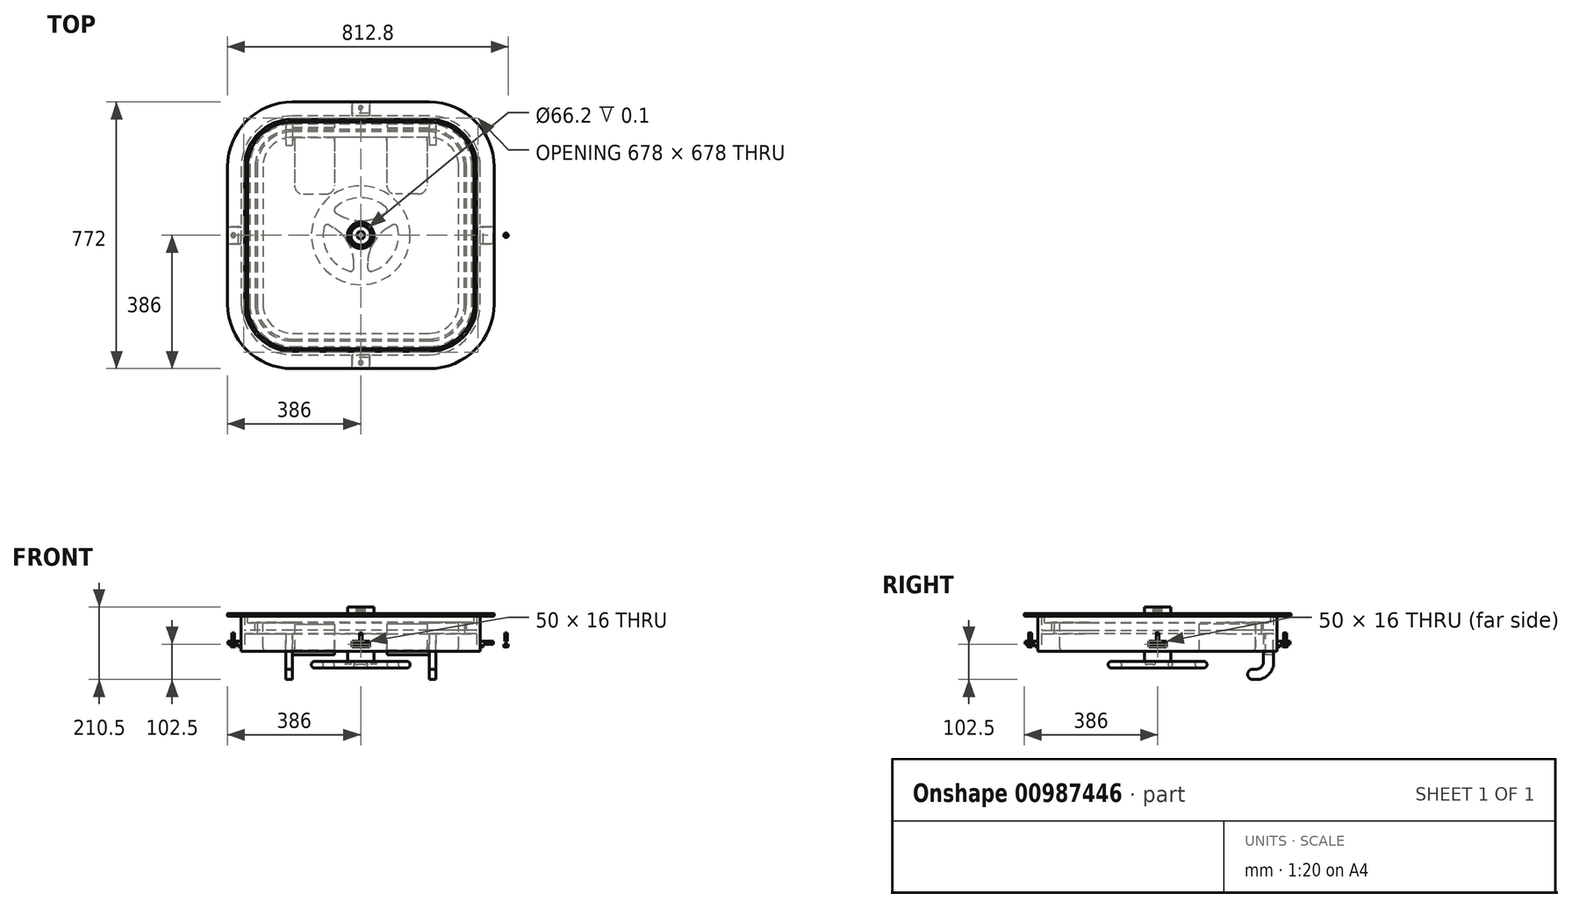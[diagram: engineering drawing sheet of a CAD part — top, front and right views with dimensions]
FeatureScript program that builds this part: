
annotation { "Feature Type Name" : "Feature", "Feature Type Description" : "" }
export const myFeature = defineFeature(function(context is Context, id is Id, definition is map)
    precondition{}
    {
        {
            var Q0;
            Q0=qCreatedBy(makeId("Top.planeOp"),FACE);
            var sketch = newSketch(context, id + "F0", { "sketchPlane" : qUnion([Q0])});
            skPoint(sketch, "E0.middle", {"position": v(0, 0) * mm});
            skPoint(sketch, "E1.visualSharp", {"position": v(-397.3, 343.3) * mm});
            skPoint(sketch, "E2.visualSharp", {"position": v(397.3, 343.3) * mm});
            skPoint(sketch, "E3.visualSharp", {"position": v(397.3, -343.3) * mm});
            skPoint(sketch, "E4.visualSharp", {"position": v(-397.3, -343.3) * mm});
            skLineSegment(sketch, "E5.1", {"start": v(-198.4, -300) * mm, "end": v(198.4, -300) * mm});
            skLineSegment(sketch, "E5.2", {"start": v(-300, -198.4) * mm, "end": v(-300, 198.4) * mm});
            skLineSegment(sketch, "E5.5", {"start": v(-198.4, 300) * mm, "end": v(198.4, 300) * mm});
            skLineSegment(sketch, "E5.7", {"start": v(300, -198.4) * mm, "end": v(300, 198.4) * mm});
            skPoint(sketch, "E6.visualSharp", {"position": v(300, -300) * mm});
            skArc(sketch, "E6.filletArc", {"start": v(198.4, -300) * mm, "mid": v(270.24, -270.24) * mm, "end": v(300, -198.4) * mm});
            skPoint(sketch, "E7.visualSharp", {"position": v(-300, -300) * mm});
            skArc(sketch, "E7.filletArc", {"start": v(-300, -198.4) * mm, "mid": v(-270.24, -270.24) * mm, "end": v(-198.4, -300) * mm});
            skPoint(sketch, "E8.visualSharp", {"position": v(-300, 300) * mm});
            skArc(sketch, "E8.filletArc", {"start": v(-198.4, 300) * mm, "mid": v(-270.24, 270.24) * mm, "end": v(-300, 198.4) * mm});
            skPoint(sketch, "E9.visualSharp", {"position": v(300, 300) * mm});
            skArc(sketch, "E9.filletArc", {"start": v(300, 198.4) * mm, "mid": v(270.24, 270.24) * mm, "end": v(198.4, 300) * mm});
            skLineSegment(sketch, "E10", {"start": v(198.4, -198.4) * mm, "end": v(-198.4, 198.4) * mm});
            skLineSegment(sketch, "E11", {"start": v(-198.4, -198.4) * mm, "end": v(198.4, 198.4) * mm});
            skSolve(sketch);
        }
        {
            var Q0;
            Q0=qCreatedBy(makeId("Front.planeOp"),FACE);
            var sketch = newSketch(context, id + "F1", { "sketchPlane" : qUnion([Q0])});
            skLineSegment(sketch, "E12", {"start": v(-346, 0) * mm, "end": v(-384, 0) * mm});
            skLineSegment(sketch, "E13", {"start": v(-386, 2) * mm, "end": v(-386, 6) * mm});
            skLineSegment(sketch, "E14", {"start": v(-384, 8) * mm, "end": v(-339, 8) * mm});
            skLineSegment(sketch, "E15", {"start": v(-336, 5) * mm, "end": v(-336, -38) * mm});
            skLineSegment(sketch, "E16", {"start": v(-333, -41) * mm, "end": v(-309, -41) * mm});
            skLineSegment(sketch, "E17", {"start": v(-306, -38) * mm, "end": v(-306, -19) * mm});
            skLineSegment(sketch, "E18", {"start": v(-303, -16) * mm, "end": v(-303, -16) * mm});
            skLineSegment(sketch, "E19", {"start": v(-300, -19) * mm, "end": v(-300, -48) * mm});
            skLineSegment(sketch, "E20", {"start": v(-303, -51) * mm, "end": v(-334, -51) * mm});
            skLineSegment(sketch, "E21", {"start": v(-336, -53) * mm, "end": v(-336, -99) * mm});
            skLineSegment(sketch, "E22", {"start": v(-339, -102) * mm, "end": v(-346, -102) * mm});
            skLineSegment(sketch, "E23", {"start": v(-346, -102) * mm, "end": v(-346, 0) * mm});
            skLineSegment(sketch, "E24", {"start": v(-300, -16) * mm, "end": v(-300, 0) * mm});
            skPoint(sketch, "E25.visualSharp", {"position": v(-300, -16) * mm});
            skArc(sketch, "E25.filletArc", {"start": v(-300, -19) * mm, "mid": v(-300.88, -16.88) * mm, "end": v(-303, -16) * mm});
            skPoint(sketch, "E26.visualSharp", {"position": v(-306, -16) * mm});
            skArc(sketch, "E26.filletArc", {"start": v(-303, -16) * mm, "mid": v(-305.12, -16.88) * mm, "end": v(-306, -19) * mm});
            skPoint(sketch, "E27.visualSharp", {"position": v(-306, -41) * mm});
            skArc(sketch, "E27.filletArc", {"start": v(-309, -41) * mm, "mid": v(-306.88, -40.12) * mm, "end": v(-306, -38) * mm});
            skPoint(sketch, "E28.visualSharp", {"position": v(-336, -41) * mm});
            skArc(sketch, "E28.filletArc", {"start": v(-336, -38) * mm, "mid": v(-335.12, -40.12) * mm, "end": v(-333, -41) * mm});
            skPoint(sketch, "E29.visualSharp", {"position": v(-300, -51) * mm});
            skArc(sketch, "E29.filletArc", {"start": v(-303, -51) * mm, "mid": v(-300.88, -50.12) * mm, "end": v(-300, -48) * mm});
            skPoint(sketch, "E30.visualSharp", {"position": v(-336, 8) * mm});
            skArc(sketch, "E30.filletArc", {"start": v(-336, 5) * mm, "mid": v(-336.88, 7.12) * mm, "end": v(-339, 8) * mm});
            skPoint(sketch, "E31.visualSharp", {"position": v(-336, -102) * mm});
            skArc(sketch, "E31.filletArc", {"start": v(-339, -102) * mm, "mid": v(-336.88, -101.12) * mm, "end": v(-336, -99) * mm});
            skPoint(sketch, "E32.visualSharp", {"position": v(-386, 8) * mm});
            skArc(sketch, "E32.filletArc", {"start": v(-384, 8) * mm, "mid": v(-385.41, 7.41) * mm, "end": v(-386, 6) * mm});
            skPoint(sketch, "E33.visualSharp", {"position": v(-386, 0) * mm});
            skArc(sketch, "E33.filletArc", {"start": v(-386, 2) * mm, "mid": v(-385.41, 0.59) * mm, "end": v(-384, 0) * mm});
            skPoint(sketch, "E34.visualSharp", {"position": v(-336, -51) * mm});
            skArc(sketch, "E34.filletArc", {"start": v(-334, -51) * mm, "mid": v(-335.41, -51.59) * mm, "end": v(-336, -53) * mm});
            skSolve(sketch);
        }
        {
            var Q0;
            Q0=makeQuery(id+"F1.imprint","IMPRINT",FACE,{"disambiguationData":[TD([[makeQuery(id+"F1.imprint","IMPRINT",EDGE,{"derivedFrom":sQuery(id+"F1.wireOp",EDGE,"E12")}),-1.0]])]});
            var Q1;
            Q1=sQuery(id+"F0.wireOp",EDGE,"E5.2");
            var Q2;
            Q2=sQuery(id+"F0.wireOp",EDGE,"E7.filletArc");
            var Q3;
            Q3=sQuery(id+"F0.wireOp",EDGE,"E5.1");
            var Q4;
            Q4=sQuery(id+"F0.wireOp",EDGE,"E6.filletArc");
            var Q5;
            Q5=sQuery(id+"F0.wireOp",EDGE,"E5.7");
            var Q6;
            Q6=sQuery(id+"F0.wireOp",EDGE,"E9.filletArc");
            var Q7;
            Q7=sQuery(id+"F0.wireOp",EDGE,"E5.5");
            var Q8;
            Q8=sQuery(id+"F0.wireOp",EDGE,"E8.filletArc");
            sweep(context, id + "F2", {"profiles" : qUnion([Q0]), "path" : qUnion([Q1, Q2, Q3, Q4, Q5, Q6, Q7, Q8])});
        }
        {
            var Q0;
            Q0=makeQuery(id+"F2.opSweep","SWEPT_FACE",FACE,{"disambiguationData":[OSD([sQuery(id+"F0.wireOp",EDGE,"E0.left"),sQuery(id+"F1.wireOp",EDGE,"E14")])]});
            var sketch = newSketch(context, id + "F3", { "sketchPlane" : qUnion([Q0])});
            skLineSegment(sketch, "E35.0", {"start": v(198.4, 328) * mm, "end": v(-198.4, 328) * mm});
            skArc(sketch, "E35.1", {"start": v(328, 198.4) * mm, "mid": v(290.04, 290.04) * mm, "end": v(198.4, 328) * mm});
            skArc(sketch, "E35.2", {"start": v(-198.4, 328) * mm, "mid": v(-290.04, 290.04) * mm, "end": v(-328, 198.4) * mm});
            skLineSegment(sketch, "E35.3", {"start": v(328, -198.4) * mm, "end": v(328, 198.4) * mm});
            skLineSegment(sketch, "E35.4", {"start": v(-328, 198.4) * mm, "end": v(-328, -198.4) * mm});
            skArc(sketch, "E35.5", {"start": v(-328, -198.4) * mm, "mid": v(-290.04, -290.04) * mm, "end": v(-198.4, -328) * mm});
            skLineSegment(sketch, "E35.6", {"start": v(-198.4, -328) * mm, "end": v(198.4, -328) * mm});
            skArc(sketch, "E35.7", {"start": v(198.4, -328) * mm, "mid": v(290.04, -290.04) * mm, "end": v(328, -198.4) * mm});
            skSolve(sketch);
        }
        {
            var Q0;
            Q0 = qSketchRegion(id + "F3", true);
            extrude(context, id + "F4", {"entities" : qUnion([Q0]), "oppositeDirection" : true, "depth" : 27 * mm, "offsetDistance" : 25 * mm});
        }
        {
            var Q0;
            Q0=qCreatedBy(makeId("Front.planeOp"),FACE);
            var sketch = newSketch(context, id + "F5", { "sketchPlane" : qUnion([Q0])});
            skLineSegment(sketch, "E36.0", {"start": v(346, -73) * mm, "end": v(346, -89) * mm});
            skLineSegment(sketch, "E37.0", {"start": v(-346, -73) * mm, "end": v(-346, -89) * mm});
            skLineSegment(sketch, "E38", {"start": v(346, -73) * mm, "end": v(384, -73) * mm});
            skLineSegment(sketch, "E39", {"start": v(384, -73) * mm, "end": v(384, -81) * mm});
            skLineSegment(sketch, "E40", {"start": v(384, -81) * mm, "end": v(354, -81) * mm});
            skLineSegment(sketch, "E41", {"start": v(354, -81) * mm, "end": v(354, -89) * mm});
            skLineSegment(sketch, "E42", {"start": v(354, -89) * mm, "end": v(346, -89) * mm});
            skLineSegment(sketch, "E43", {"start": v(-346, -73) * mm, "end": v(-384, -73) * mm});
            skLineSegment(sketch, "E44", {"start": v(-384, -73) * mm, "end": v(-384, -81) * mm});
            skLineSegment(sketch, "E45", {"start": v(-384, -81) * mm, "end": v(-354, -81) * mm});
            skLineSegment(sketch, "E46", {"start": v(-354, -81) * mm, "end": v(-354, -89) * mm});
            skLineSegment(sketch, "E47", {"start": v(-354, -89) * mm, "end": v(-346, -89) * mm});
            skPoint(sketch, "E48.orphan", {"position": v(-346, 0) * mm});
            skPoint(sketch, "E49.orphan", {"position": v(-346, -102) * mm});
            skPoint(sketch, "E50.orphan", {"position": v(346, 0) * mm});
            skPoint(sketch, "E51.orphan", {"position": v(346, -102) * mm});
            skSolve(sketch);
        }
        {
            var Q0;
            Q0 = qSketchRegion(id + "F5", true);
            extrude(context, id + "F6", {"entities" : qUnion([Q0]), "operationType" : NewBodyOperationType.ADD, "depth" : 25 * mm, "offsetDistance" : 25 * mm, "hasSecondDirection" : true, "secondDirectionOppositeDirection" : true, "secondDirectionDepth" : 25 * mm});
        }
        {
            var Q0;
            Q0=qCreatedBy(makeId("Right.planeOp"),FACE);
            var sketch = newSketch(context, id + "F7", { "sketchPlane" : qUnion([Q0])});
            skLineSegment(sketch, "E52.0", {"start": v(-346, 0) * mm, "end": v(-346, -102) * mm});
            skLineSegment(sketch, "E53.0", {"start": v(346, 0) * mm, "end": v(346, -102) * mm});
            skLineSegment(sketch, "E54", {"start": v(-346, -73) * mm, "end": v(-384, -73) * mm});
            skLineSegment(sketch, "E55", {"start": v(-384, -73) * mm, "end": v(-384, -81) * mm});
            skLineSegment(sketch, "E56", {"start": v(-384, -81) * mm, "end": v(-354, -81) * mm});
            skLineSegment(sketch, "E57", {"start": v(-354, -81) * mm, "end": v(-354, -89) * mm});
            skLineSegment(sketch, "E58", {"start": v(-354, -89) * mm, "end": v(-346, -89) * mm});
            skLineSegment(sketch, "E59", {"start": v(346, -73) * mm, "end": v(384, -73) * mm});
            skLineSegment(sketch, "E60", {"start": v(384, -73) * mm, "end": v(384, -81) * mm});
            skLineSegment(sketch, "E61", {"start": v(384, -81) * mm, "end": v(354, -81) * mm});
            skLineSegment(sketch, "E62", {"start": v(354, -81) * mm, "end": v(354, -89) * mm});
            skLineSegment(sketch, "E63", {"start": v(354, -89) * mm, "end": v(346, -89) * mm});
            skSolve(sketch);
        }
        {
            var Q0;
            Q0 = qSketchRegion(id + "F7", true);
            extrude(context, id + "F8", {"entities" : qUnion([Q0]), "operationType" : NewBodyOperationType.ADD, "depth" : 25 * mm, "offsetDistance" : 25 * mm, "hasSecondDirection" : true, "secondDirectionOppositeDirection" : true, "secondDirectionDepth" : 25 * mm});
        }
        {
            var Q0;
            Q0=makeQuery(id+"F8.opExtrude","SWEPT_FACE",FACE,{"disambiguationData":[OSD([sQuery(id+"F7.wireOp",EDGE,"E56")])]});
            var sketch = newSketch(context, id + "F9", { "sketchPlane" : qUnion([Q0])});
            skCircle(sketch, "E64", {"center": v(0, 369) * mm, "radius": 6.5 * mm});
            skPoint(sketch, "E64.centerSnap0", {"position": v(-25, 369) * mm});
            skPoint(sketch, "E64.centerSnap1", {"position": v(0, 384) * mm});
            skLineSegment(sketch, "E65", {"start": v(-369, 25) * mm, "end": v(-369, 0) * mm});
            skCircle(sketch, "E66", {"center": v(-369, 0) * mm, "radius": 6.5 * mm});
            skLineSegment(sketch, "E67", {"start": v(-300, 0) * mm, "end": v(0, 0) * mm});
            skCircle(sketch, "E68.MirrorC", {"center": v(420.3, 0) * mm, "radius": 6.5 * mm});
            skCircle(sketch, "E69.MirrorC", {"center": v(0, -369) * mm, "radius": 6.5 * mm});
            skLineSegment(sketch, "E70", {"start": v(0, 0) * mm, "end": v(0, 300) * mm});
            skSolve(sketch);
        }
        {
            var Q0;
            Q0 = qSketchRegion(id + "F9", true);
            extrude(context, id + "F10", {"entities" : qUnion([Q0]), "operationType" : NewBodyOperationType.ADD, "depth" : 8 * mm, "offsetDistance" : 25 * mm});
        }
        {
            var Q0;
            Q0=makeQuery(id+"F10.opExtrude","CAP_EDGE",EDGE,{"disambiguationData":[OSD([sQuery(id+"F9.wireOp",EDGE,"E66")])],"isStart":false});
            var Q1;
            Q1=makeQuery(id+"F10.opExtrude","CAP_EDGE",EDGE,{"disambiguationData":[OSD([sQuery(id+"F9.wireOp",EDGE,"E64")])],"isStart":false});
            var Q2;
            Q2=makeQuery(id+"F10.opExtrude","CAP_EDGE",EDGE,{"disambiguationData":[OSD([sQuery(id+"F9.wireOp",EDGE,"E68.MirrorC")])],"isStart":false});
            var Q3;
            Q3=makeQuery(id+"F10.opExtrude","CAP_EDGE",EDGE,{"disambiguationData":[OSD([sQuery(id+"F9.wireOp",EDGE,"E69.MirrorC")])],"isStart":false});
            chamfer(context, id + "F11", {"entities" : qUnion([Q0, Q1, Q2, Q3]), "width" : 1 * mm, "tangentPropagation" : true});
        }
        {
            var Q0;
            Q0=makeQuery(id+"F8.opExtrude","SWEPT_FACE",FACE,{"disambiguationData":[OSD([sQuery(id+"F7.wireOp",EDGE,"E59")])]});
            var sketch = newSketch(context, id + "F12", { "sketchPlane" : qUnion([Q0])});
            skCircle(sketch, "E71", {"center": v(0, 369) * mm, "radius": 4 * mm});
            skCircle(sketch, "E72", {"center": v(-369, 0) * mm, "radius": 4 * mm});
            skCircle(sketch, "E73", {"center": v(0, -369) * mm, "radius": 4 * mm});
            skCircle(sketch, "E74", {"center": v(420.3, 0) * mm, "radius": 4 * mm});
            skSolve(sketch);
        }
        {
            var Q0;
            Q0 = qSketchRegion(id + "F12", true);
            extrude(context, id + "F13", {"entities" : qUnion([Q0]), "operationType" : NewBodyOperationType.ADD, "depth" : 25 * mm, "offsetDistance" : 25 * mm});
        }
        {
            var Q0;
            Q0=makeQuery(id+"F4.opExtrude","CAP_FACE",FACE,{"disambiguationData":[OSD([sQuery(id+"F3.wireOp",EDGE,"E35.0"),sQuery(id+"F3.wireOp",EDGE,"E35.1"),sQuery(id+"F3.wireOp",EDGE,"E35.2"),sQuery(id+"F3.wireOp",EDGE,"E35.3"),sQuery(id+"F3.wireOp",EDGE,"E35.4"),sQuery(id+"F3.wireOp",EDGE,"E35.5"),sQuery(id+"F3.wireOp",EDGE,"E35.6"),sQuery(id+"F3.wireOp",EDGE,"E35.7")])],"isStart":false});
            shell(context, id + "F14", {"entities" : qUnion([Q0]), "thickness" : 6.35 * mm});
        }
        {
            var Q0;
            Q0=makeQuery(id+"F14.opShell","OFFSET_FACE",FACE,{"disambiguationData":[OSD([sQuery(id+"F3.wireOp",EDGE,"E35.0"),sQuery(id+"F3.wireOp",EDGE,"E35.1"),sQuery(id+"F3.wireOp",EDGE,"E35.2"),sQuery(id+"F3.wireOp",EDGE,"E35.3"),sQuery(id+"F3.wireOp",EDGE,"E35.4"),sQuery(id+"F3.wireOp",EDGE,"E35.5"),sQuery(id+"F3.wireOp",EDGE,"E35.6"),sQuery(id+"F3.wireOp",EDGE,"E35.7")])]});
            var sketch = newSketch(context, id + "F15", { "sketchPlane" : qUnion([Q0])});
            skLineSegment(sketch, "E75.0", {"start": v(-283.55, -198.4) * mm, "end": v(-283.55, 198.4) * mm});
            skArc(sketch, "E75.1", {"start": v(-198.4, -283.55) * mm, "mid": v(-258.61, -258.61) * mm, "end": v(-283.55, -198.4) * mm});
            skArc(sketch, "E75.2", {"start": v(-283.55, 198.4) * mm, "mid": v(-258.61, 258.61) * mm, "end": v(-198.4, 283.55) * mm});
            skLineSegment(sketch, "E75.3", {"start": v(198.4, -283.55) * mm, "end": v(-198.4, -283.55) * mm});
            skLineSegment(sketch, "E75.4", {"start": v(-198.4, 283.55) * mm, "end": v(198.4, 283.55) * mm});
            skArc(sketch, "E75.5", {"start": v(198.4, 283.55) * mm, "mid": v(258.61, 258.61) * mm, "end": v(283.55, 198.4) * mm});
            skLineSegment(sketch, "E75.6", {"start": v(283.55, 198.4) * mm, "end": v(283.55, -198.4) * mm});
            skArc(sketch, "E75.7", {"start": v(283.55, -198.4) * mm, "mid": v(258.61, -258.61) * mm, "end": v(198.4, -283.55) * mm});
            skSolve(sketch);
        }
        {
            var Q0;
            Q0 = qSketchRegion(id + "F15", true);
            extrude(context, id + "F16", {"entities" : qUnion([Q0]), "operationType" : NewBodyOperationType.ADD, "depth" : 102 * mm, "offsetDistance" : 25 * mm});
        }
        {
            var Q0;
            Q0=makeQuery(id+"F14.opShell","OFFSET_FACE",FACE,{"disambiguationData":[OSD([sQuery(id+"F3.wireOp",EDGE,"E35.0"),sQuery(id+"F3.wireOp",EDGE,"E35.1"),sQuery(id+"F3.wireOp",EDGE,"E35.2"),sQuery(id+"F3.wireOp",EDGE,"E35.3"),sQuery(id+"F3.wireOp",EDGE,"E35.4"),sQuery(id+"F3.wireOp",EDGE,"E35.5"),sQuery(id+"F3.wireOp",EDGE,"E35.6"),sQuery(id+"F3.wireOp",EDGE,"E35.7")])]});
            var sketch = newSketch(context, id + "F17", { "sketchPlane" : qUnion([Q0])});
            skLineSegment(sketch, "E76.0.0", {"start": v(198.4, 321.65) * mm, "end": v(-198.4, 321.65) * mm});
            skArc(sketch, "E76.0.1", {"start": v(-198.4, 321.65) * mm, "mid": v(-285.55, 285.55) * mm, "end": v(-321.65, 198.4) * mm});
            skLineSegment(sketch, "E76.0.2", {"start": v(-321.65, 198.4) * mm, "end": v(-321.65, -198.4) * mm});
            skArc(sketch, "E76.0.3", {"start": v(-321.65, -198.4) * mm, "mid": v(-285.55, -285.55) * mm, "end": v(-198.4, -321.65) * mm});
            skLineSegment(sketch, "E76.0.4", {"start": v(-198.4, -321.65) * mm, "end": v(198.4, -321.65) * mm});
            skArc(sketch, "E76.0.5", {"start": v(198.4, -321.65) * mm, "mid": v(285.55, -285.55) * mm, "end": v(321.65, -198.4) * mm});
            skLineSegment(sketch, "E76.0.6", {"start": v(321.65, -198.4) * mm, "end": v(321.65, 198.4) * mm});
            skArc(sketch, "E76.0.7", {"start": v(321.65, 198.4) * mm, "mid": v(285.55, 285.55) * mm, "end": v(198.4, 321.65) * mm});
            skLineSegment(sketch, "E77.0", {"start": v(-283.55, -198.4) * mm, "end": v(-283.55, 198.4) * mm});
            skArc(sketch, "E78.0", {"start": v(-198.4, -283.55) * mm, "mid": v(-258.61, -258.61) * mm, "end": v(-283.55, -198.4) * mm});
            skLineSegment(sketch, "E79.0", {"start": v(198.4, -283.55) * mm, "end": v(-198.4, -283.55) * mm});
            skArc(sketch, "E80.0", {"start": v(283.55, -198.4) * mm, "mid": v(258.61, -258.61) * mm, "end": v(198.4, -283.55) * mm});
            skLineSegment(sketch, "E81.0", {"start": v(283.55, 198.4) * mm, "end": v(283.55, -198.4) * mm});
            skArc(sketch, "E82.0", {"start": v(198.4, 283.55) * mm, "mid": v(258.61, 258.61) * mm, "end": v(283.55, 198.4) * mm});
            skLineSegment(sketch, "E83.0", {"start": v(-198.4, 283.55) * mm, "end": v(198.4, 283.55) * mm});
            skSolve(sketch);
        }
        {
            var Q0;
            Q0 = qSketchRegion(id + "F17", true);
            extrude(context, id + "F18", {"entities" : qUnion([Q0]), "operationType" : NewBodyOperationType.ADD, "depth" : 19 * mm, "offsetDistance" : 25 * mm});
        }
        {
            var Q0;
            Q0=makeQuery(id+"F16.opExtrude","CAP_FACE",FACE,{"disambiguationData":[OSD([sQuery(id+"F15.wireOp",EDGE,"E75.0"),sQuery(id+"F15.wireOp",EDGE,"E75.1"),sQuery(id+"F15.wireOp",EDGE,"E75.2"),sQuery(id+"F15.wireOp",EDGE,"E75.3"),sQuery(id+"F15.wireOp",EDGE,"E75.4"),sQuery(id+"F15.wireOp",EDGE,"E75.5"),sQuery(id+"F15.wireOp",EDGE,"E75.6"),sQuery(id+"F15.wireOp",EDGE,"E75.7")])],"isStart":false});
            var Q1;
            Q1=makeQuery(id+"F4.opExtrude","CAP_FACE",FACE,{"disambiguationData":[OSD([sQuery(id+"F3.wireOp",EDGE,"E35.0"),sQuery(id+"F3.wireOp",EDGE,"E35.1"),sQuery(id+"F3.wireOp",EDGE,"E35.2"),sQuery(id+"F3.wireOp",EDGE,"E35.3"),sQuery(id+"F3.wireOp",EDGE,"E35.4"),sQuery(id+"F3.wireOp",EDGE,"E35.5"),sQuery(id+"F3.wireOp",EDGE,"E35.6"),sQuery(id+"F3.wireOp",EDGE,"E35.7")])],"isStart":true});
            fillet(context, id + "F19", {"entities" : qUnion([Q0, Q1]), "radius" : 10 * mm, "tangentPropagation" : true, "allowEdgeOverflow" : false});
        }
        {
            var Q0;
            Q0=makeQuery(id+"F16.opExtrude","CAP_FACE",FACE,{"disambiguationData":[OSD([sQuery(id+"F15.wireOp",EDGE,"E75.0"),sQuery(id+"F15.wireOp",EDGE,"E75.1"),sQuery(id+"F15.wireOp",EDGE,"E75.2"),sQuery(id+"F15.wireOp",EDGE,"E75.3"),sQuery(id+"F15.wireOp",EDGE,"E75.4"),sQuery(id+"F15.wireOp",EDGE,"E75.5"),sQuery(id+"F15.wireOp",EDGE,"E75.6"),sQuery(id+"F15.wireOp",EDGE,"E75.7")])],"isStart":false});
            var sketch = newSketch(context, id + "F20", { "sketchPlane" : qUnion([Q0])});
            skLineSegment(sketch, "E84", {"start": v(0, -273.55) * mm, "end": v(0, 0) * mm});
            skLineSegment(sketch, "E85.bottom", {"start": v(-191.55, -283.55) * mm, "end": v(-75.55, -283.55) * mm});
            skLineSegment(sketch, "E85.top", {"start": v(-166.55, -119.55) * mm, "end": v(-100.55, -119.55) * mm});
            skLineSegment(sketch, "E85.left", {"start": v(-191.55, -283.55) * mm, "end": v(-191.55, -144.55) * mm});
            skLineSegment(sketch, "E85.right", {"start": v(-75.55, -283.55) * mm, "end": v(-75.55, -144.55) * mm});
            skPoint(sketch, "E86.visualSharp", {"position": v(-191.55, -119.55) * mm});
            skArc(sketch, "E86.filletArc", {"start": v(-166.55, -119.55) * mm, "mid": v(-184.23, -126.87) * mm, "end": v(-191.55, -144.55) * mm});
            skPoint(sketch, "E87.visualSharp", {"position": v(-75.55, -119.55) * mm});
            skArc(sketch, "E87.filletArc", {"start": v(-75.55, -144.55) * mm, "mid": v(-82.87, -126.87) * mm, "end": v(-100.55, -119.55) * mm});
            skLineSegment(sketch, "E88.MirrorCS", {"start": v(191.55, -283.55) * mm, "end": v(75.55, -283.55) * mm});
            skLineSegment(sketch, "E89.MirrorCS", {"start": v(75.55, -283.55) * mm, "end": v(75.55, -144.55) * mm});
            skArc(sketch, "E90.MirrorCS", {"start": v(75.55, -144.55) * mm, "mid": v(82.87, -126.87) * mm, "end": v(100.55, -119.55) * mm});
            skLineSegment(sketch, "E91.MirrorCS", {"start": v(166.55, -119.55) * mm, "end": v(100.55, -119.55) * mm});
            skArc(sketch, "E92.MirrorCS", {"start": v(166.55, -119.55) * mm, "mid": v(184.23, -126.87) * mm, "end": v(191.55, -144.55) * mm});
            skLineSegment(sketch, "E93.MirrorCS", {"start": v(191.55, -283.55) * mm, "end": v(191.55, -144.55) * mm});
            skSolve(sketch);
        }
        {
            var Q0;
            Q0 = qSketchRegion(id + "F20", true);
            extrude(context, id + "F21", {"entities" : qUnion([Q0]), "operationType" : NewBodyOperationType.REMOVE, "oppositeDirection" : true, "depth" : 78 * mm, "offsetDistance" : 25 * mm});
        }
        {
            var Q0;
            Q0=makeQuery(id+"F4.opExtrude","CAP_FACE",FACE,{"disambiguationData":[OSD([sQuery(id+"F3.wireOp",EDGE,"E35.0"),sQuery(id+"F3.wireOp",EDGE,"E35.1"),sQuery(id+"F3.wireOp",EDGE,"E35.2"),sQuery(id+"F3.wireOp",EDGE,"E35.3"),sQuery(id+"F3.wireOp",EDGE,"E35.4"),sQuery(id+"F3.wireOp",EDGE,"E35.5"),sQuery(id+"F3.wireOp",EDGE,"E35.6"),sQuery(id+"F3.wireOp",EDGE,"E35.7")])],"isStart":true});
            var sketch = newSketch(context, id + "F22", { "sketchPlane" : qUnion([Q0])});
            skCircle(sketch, "E94", {"center": v(0, 0) * mm, "radius": 38.1 * mm});
            skSolve(sketch);
        }
        {
            var Q0;
            Q0 = qSketchRegion(id + "F22", true);
            extrude(context, id + "F23", {"entities" : qUnion([Q0]), "operationType" : NewBodyOperationType.ADD, "depth" : 19 * mm, "offsetDistance" : 25 * mm});
        }
        {
            var Q0;
            Q0=makeQuery(id+"F23.opExtrude","CAP_FACE",FACE,{"disambiguationData":[OSD([sQuery(id+"F22.wireOp",EDGE,"E94")])],"isStart":false});
            var sketch = newSketch(context, id + "F24", { "sketchPlane" : qUnion([Q0])});
            skLineSegment(sketch, "E95.bottom", {"start": v(9, -9) * mm, "end": v(3.73, -9) * mm});
            skLineSegment(sketch, "E95.top", {"start": v(9, 9) * mm, "end": v(3.73, 9) * mm});
            skLineSegment(sketch, "E95.left", {"start": v(9, -9) * mm, "end": v(9, -3.73) * mm});
            skLineSegment(sketch, "E95.right", {"start": v(-9, -9) * mm, "end": v(-9, -3.73) * mm});
            skPoint(sketch, "E95.middle", {"position": v(0, 0) * mm});
            skLineSegment(sketch, "E96.bottom", {"start": v(12.73, 0) * mm, "end": v(9, -3.73) * mm});
            skLineSegment(sketch, "E96.top", {"start": v(0, 12.73) * mm, "end": v(-3.73, 9) * mm});
            skLineSegment(sketch, "E96.left", {"start": v(12.73, 0) * mm, "end": v(9, 3.73) * mm});
            skLineSegment(sketch, "E96.right", {"start": v(0, -12.73) * mm, "end": v(-3.73, -9) * mm});
            skLineSegment(sketch, "E97.trimOffspring", {"start": v(-9, 3.73) * mm, "end": v(-12.73, 0) * mm});
            skLineSegment(sketch, "E98.trimOffspring", {"start": v(-3.73, 9) * mm, "end": v(-9, 9) * mm});
            skLineSegment(sketch, "E99.trimOffspring", {"start": v(9, 3.73) * mm, "end": v(9, 9) * mm});
            skLineSegment(sketch, "E100.trimOffspring", {"start": v(3.73, -9) * mm, "end": v(0, -12.73) * mm});
            skLineSegment(sketch, "E101.trimOffspring", {"start": v(-3.73, -9) * mm, "end": v(-9, -9) * mm});
            skLineSegment(sketch, "E102.trimOffspring", {"start": v(-9, -3.73) * mm, "end": v(-12.73, 0) * mm});
            skLineSegment(sketch, "E103.trimOffspring", {"start": v(-9, 3.73) * mm, "end": v(-9, 9) * mm});
            skLineSegment(sketch, "E104.trimOffspring", {"start": v(3.73, 9) * mm, "end": v(0, 12.73) * mm});
            skSolve(sketch);
        }
        {
            var Q0;
            Q0 = qSketchRegion(id + "F24", true);
            extrude(context, id + "F25", {"entities" : qUnion([Q0]), "operationType" : NewBodyOperationType.REMOVE, "oppositeDirection" : true, "depth" : 18 * mm, "offsetDistance" : 25 * mm});
        }
        {
            var Q0;
            Q0=makeQuery(id+"F23.opExtrude","CAP_FACE",FACE,{"disambiguationData":[OSD([sQuery(id+"F22.wireOp",EDGE,"E94")])],"isStart":false});
            var sketch = newSketch(context, id + "F26", { "sketchPlane" : qUnion([Q0])});
            skCircle(sketch, "E105.0", {"center": v(0, 0) * mm, "radius": 33.1 * mm});
            skCircle(sketch, "E106", {"center": v(0, 0) * mm, "radius": 28.5 * mm});
            skSolve(sketch);
        }
        {
            var Q0;
            Q0 = qSketchRegion(id + "F26", true);
            extrude(context, id + "F27", {"entities" : qUnion([Q0]), "operationType" : NewBodyOperationType.REMOVE, "oppositeDirection" : true, "depth" : .1 * mm, "offsetDistance" : 25 * mm});
        }
        {
            var Q0;
            Q0=makeQuery(id+"F16.opExtrude","CAP_FACE",FACE,{"disambiguationData":[OSD([sQuery(id+"F15.wireOp",EDGE,"E75.0"),sQuery(id+"F15.wireOp",EDGE,"E75.1"),sQuery(id+"F15.wireOp",EDGE,"E75.2"),sQuery(id+"F15.wireOp",EDGE,"E75.3"),sQuery(id+"F15.wireOp",EDGE,"E75.4"),sQuery(id+"F15.wireOp",EDGE,"E75.5"),sQuery(id+"F15.wireOp",EDGE,"E75.6"),sQuery(id+"F15.wireOp",EDGE,"E75.7")])],"isStart":false});
            var sketch = newSketch(context, id + "F28", { "sketchPlane" : qUnion([Q0])});
            skCircle(sketch, "E107", {"center": v(0, 0) * mm, "radius": 38.1 * mm});
            skSolve(sketch);
        }
        {
            var Q0;
            Q0 = qSketchRegion(id + "F28", true);
            extrude(context, id + "F29", {"entities" : qUnion([Q0]), "operationType" : NewBodyOperationType.ADD, "depth" : 30.48 * mm, "offsetDistance" : 25 * mm});
        }
        {
            var Q0;
            Q0=makeQuery(id+"F29.opExtrude","CAP_FACE",FACE,{"disambiguationData":[OSD([sQuery(id+"F28.wireOp",EDGE,"E107")])],"isStart":false});
            var sketch = newSketch(context, id + "F30", { "sketchPlane" : qUnion([Q0])});
            skArc(sketch, "E108", {"start": v(-33.03, 103.87) * mm, "mid": v(-94.4, 54.5) * mm, "end": v(-106.47, -23.33) * mm});
            skCircle(sketch, "E109", {"center": v(0, 0) * mm, "radius": 143 * mm});
            skLineSegment(sketch, "E110", {"start": v(0, 109) * mm, "end": v(0, 0) * mm});
            skLineSegment(sketch, "E111", {"start": v(0, 0) * mm, "end": v(-94.4, -54.5) * mm});
            skLineSegment(sketch, "E112", {"start": v(-20, 94.35) * mm, "end": v(-20, 82.56) * mm});
            skLineSegment(sketch, "E113", {"start": v(-91.7, -29.85) * mm, "end": v(-81.5, -23.96) * mm});
            skArc(sketch, "E114", {"start": v(-81.5, -23.96) * mm, "mid": v(-36.48, 21.06) * mm, "end": v(-20, 82.56) * mm});
            skPoint(sketch, "E115.visualSharp", {"position": v(-20, 107.15) * mm});
            skArc(sketch, "E115.filletArc", {"start": v(-20, 94.35) * mm, "mid": v(-24.1, 102.42) * mm, "end": v(-33.03, 103.87) * mm});
            skPoint(sketch, "E116.visualSharp", {"position": v(-102.8, -36.25) * mm});
            skArc(sketch, "E116.filletArc", {"start": v(-106.47, -23.33) * mm, "mid": v(-100.74, -30.34) * mm, "end": v(-91.7, -29.85) * mm});
            skArc(sketch, "E117.1.0", {"start": v(-73.44, -80.54) * mm, "mid": v(0, -109) * mm, "end": v(73.44, -80.54) * mm});
            skArc(sketch, "E117.1.1", {"start": v(-71.7, -64.5) * mm, "mid": v(-76.65, -72.08) * mm, "end": v(-73.44, -80.54) * mm});
            skLineSegment(sketch, "E117.1.2", {"start": v(-71.7, -64.5) * mm, "end": v(-61.5, -58.6) * mm});
            skArc(sketch, "E117.1.3", {"start": v(61.5, -58.6) * mm, "mid": v(0, -42.12) * mm, "end": v(-61.5, -58.6) * mm});
            skLineSegment(sketch, "E117.1.4", {"start": v(71.7, -64.5) * mm, "end": v(61.5, -58.6) * mm});
            skArc(sketch, "E117.1.5", {"start": v(73.44, -80.54) * mm, "mid": v(76.65, -72.08) * mm, "end": v(71.7, -64.5) * mm});
            skArc(sketch, "E117.2.0", {"start": v(106.47, -23.33) * mm, "mid": v(94.4, 54.5) * mm, "end": v(33.03, 103.87) * mm});
            skArc(sketch, "E117.2.1", {"start": v(91.7, -29.85) * mm, "mid": v(100.74, -30.34) * mm, "end": v(106.47, -23.33) * mm});
            skLineSegment(sketch, "E117.2.2", {"start": v(91.7, -29.85) * mm, "end": v(81.5, -23.96) * mm});
            skArc(sketch, "E117.2.3", {"start": v(20, 82.56) * mm, "mid": v(36.48, 21.06) * mm, "end": v(81.5, -23.96) * mm});
            skLineSegment(sketch, "E117.2.4", {"start": v(20, 94.35) * mm, "end": v(20, 82.56) * mm});
            skArc(sketch, "E117.2.5", {"start": v(33.03, 103.87) * mm, "mid": v(24.1, 102.42) * mm, "end": v(20, 94.35) * mm});
            skSolve(sketch);
        }
        {
            var Q0;
            {var subQ0=sQuery(id+"F30.wireOp",EDGE,"E111");var subQ1=sQuery(id+"F30.wireOp",EDGE,"E110");var subQ2=makeQuery(id+"F30.imprint","INTERSECT",VERTEX,{"derivedFrom":[subQ1,subQ0]});Q0=makeQuery(id+"F30.imprint","IMPRINT",FACE,{"disambiguationData":[TD([[makeQuery(id+"F30.imprint","IMPRINT",EDGE,{"disambiguationData":[TD([[subQ2,1.0]])],"derivedFrom":subQ1}),-1.0]])]});}
            var Q1;
            {var subQ0=sQuery(id+"F30.wireOp",EDGE,"E111");var subQ1=sQuery(id+"F30.wireOp",EDGE,"E110");var subQ2=makeQuery(id+"F30.imprint","INTERSECT",VERTEX,{"derivedFrom":[subQ1,subQ0]});Q1=makeQuery(id+"F30.imprint","IMPRINT",FACE,{"disambiguationData":[TD([[makeQuery(id+"F30.imprint","IMPRINT",EDGE,{"disambiguationData":[TD([[subQ2,1.0]])],"derivedFrom":subQ1}),1.0]])]});}
            var Q2;
            Q2=makeQuery(id+"F30.imprint","IMPRINT",FACE,{"disambiguationData":[TD([[makeQuery(id+"F30.imprint","IMPRINT",EDGE,{"derivedFrom":sQuery(id+"F30.wireOp",EDGE,"E108")}),-1.0]])]});
            extrude(context, id + "F31", {"entities" : qUnion([Q0, Q1, Q2]), "operationType" : NewBodyOperationType.ADD, "depth" : 19 * mm, "offsetDistance" : 25 * mm});
        }
        {
            var Q0;
            Q0=makeQuery(id+"F31.opExtrude","CAP_EDGE",EDGE,{"disambiguationData":[OSD([sQuery(id+"F30.wireOp",EDGE,"E109")])],"isStart":true});
            var Q1;
            Q1=makeQuery(id+"F31.opExtrude","CAP_EDGE",EDGE,{"disambiguationData":[OSD([sQuery(id+"F30.wireOp",EDGE,"E117.2.0")])],"isStart":true});
            var Q2;
            Q2=makeQuery(id+"F31.opExtrude","CAP_EDGE",EDGE,{"disambiguationData":[OSD([sQuery(id+"F30.wireOp",EDGE,"E108")])],"isStart":true});
            var Q3;
            Q3=makeQuery(id+"F31.opExtrude","CAP_EDGE",EDGE,{"disambiguationData":[OSD([sQuery(id+"F30.wireOp",EDGE,"E117.1.3")])],"isStart":true});
            var Q4;
            Q4=makeQuery(id+"F31.opExtrude","CAP_FACE",FACE,{"disambiguationData":[OSD([sQuery(id+"F30.wireOp",EDGE,"E108"),sQuery(id+"F30.wireOp",EDGE,"E109"),sQuery(id+"F30.wireOp",EDGE,"E112"),sQuery(id+"F30.wireOp",EDGE,"E113"),sQuery(id+"F30.wireOp",EDGE,"E114"),sQuery(id+"F30.wireOp",EDGE,"E115.filletArc"),sQuery(id+"F30.wireOp",EDGE,"E116.filletArc"),sQuery(id+"F30.wireOp",EDGE,"E117.1.0"),sQuery(id+"F30.wireOp",EDGE,"E117.1.1"),sQuery(id+"F30.wireOp",EDGE,"E117.1.2"),sQuery(id+"F30.wireOp",EDGE,"E117.1.3"),sQuery(id+"F30.wireOp",EDGE,"E117.1.4"),sQuery(id+"F30.wireOp",EDGE,"E117.1.5"),sQuery(id+"F30.wireOp",EDGE,"E117.2.0"),sQuery(id+"F30.wireOp",EDGE,"E117.2.1"),sQuery(id+"F30.wireOp",EDGE,"E117.2.2"),sQuery(id+"F30.wireOp",EDGE,"E117.2.3"),sQuery(id+"F30.wireOp",EDGE,"E117.2.4"),sQuery(id+"F30.wireOp",EDGE,"E117.2.5")])],"isStart":false});
            fillet(context, id + "F32", {"entities" : qUnion([Q0, Q1, Q2, Q3, Q4]), "radius" : 9 * mm, "tangentPropagation" : true, "allowEdgeOverflow" : false});
        }
        {
            var Q0;
            Q0=makeQuery(id+"F2.opSweep","SWEPT_FACE",FACE,{"disambiguationData":[OSD([sQuery(id+"F0.wireOp",EDGE,"E5.2"),sQuery(id+"F1.wireOp",EDGE,"E20")])]});
            var sketch = newSketch(context, id + "F33", { "sketchPlane" : qUnion([Q0])});
            skLineSegment(sketch, "E118", {"start": v(0, 0) * mm, "end": v(0, -303) * mm});
            skLineSegment(sketch, "E119.bottom", {"start": v(-76.4, -336) * mm, "end": v(-198.4, -336) * mm});
            skLineSegment(sketch, "E119.top", {"start": v(-76.4, -312) * mm, "end": v(-198.4, -312) * mm});
            skLineSegment(sketch, "E119.left", {"start": v(-76.4, -336) * mm, "end": v(-76.4, -312) * mm});
            skLineSegment(sketch, "E119.right", {"start": v(-198.4, -336) * mm, "end": v(-198.4, -312) * mm});
            skLineSegment(sketch, "E120.MirrorCS", {"start": v(76.4, -336) * mm, "end": v(198.4, -336) * mm});
            skLineSegment(sketch, "E121.MirrorCS", {"start": v(76.4, -336) * mm, "end": v(76.4, -312) * mm});
            skLineSegment(sketch, "E122.MirrorCS", {"start": v(76.4, -312) * mm, "end": v(198.4, -312) * mm});
            skLineSegment(sketch, "E123.MirrorCS", {"start": v(198.4, -336) * mm, "end": v(198.4, -312) * mm});
            skSolve(sketch);
        }
        {
            var Q0;
            Q0 = qSketchRegion(id + "F33", true);
            extrude(context, id + "F34", {"entities" : qUnion([Q0]), "operationType" : NewBodyOperationType.ADD, "depth" : 61 * mm, "offsetDistance" : 25 * mm});
        }
        {
            var Q0;
            Q0=makeQuery(id+"F34.opExtrude","SWEPT_FACE",FACE,{"disambiguationData":[OSD([sQuery(id+"F33.wireOp",EDGE,"E119.right")])]});
            var sketch = newSketch(context, id + "F35", { "sketchPlane" : qUnion([Q0])});
            skArc(sketch, "E124.0", {"start": v(-336, -53) * mm, "mid": v(-335.41, -51.59) * mm, "end": v(-334, -51) * mm});
            skLineSegment(sketch, "E125.0", {"start": v(-334, -51) * mm, "end": v(-312, -51) * mm});
            skLineSegment(sketch, "E126.0.0", {"start": v(-306, -51) * mm, "end": v(-334, -51) * mm});
            skLineSegment(sketch, "E126.0.2", {"start": v(-336, -133.5) * mm, "end": v(-336, -53) * mm});
            skPoint(sketch, "E127.orphan", {"position": v(-336, -99) * mm});
            skLineSegment(sketch, "E128", {"start": v(-306, -51) * mm, "end": v(-306, -133.5) * mm});
            skLineSegment(sketch, "E129", {"start": v(-286, -153.5) * mm, "end": v(-275.7, -153.5) * mm});
            skLineSegment(sketch, "E130", {"start": v(-260.7, -168.5) * mm, "end": v(-260.7, -168.5) * mm});
            skLineSegment(sketch, "E131", {"start": v(-275.7, -183.5) * mm, "end": v(-286, -183.5) * mm});
            skPoint(sketch, "E132.visualSharp", {"position": v(-306, -153.5) * mm});
            skArc(sketch, "E132.filletArc", {"start": v(-306, -133.5) * mm, "mid": v(-300.14, -147.64) * mm, "end": v(-286, -153.5) * mm});
            skPoint(sketch, "E133.visualSharp", {"position": v(-336, -183.5) * mm});
            skArc(sketch, "E133.filletArc", {"start": v(-336, -133.5) * mm, "mid": v(-321.36, -168.86) * mm, "end": v(-286, -183.5) * mm});
            skPoint(sketch, "E134.visualSharp", {"position": v(-260.7, -153.5) * mm});
            skArc(sketch, "E134.filletArc", {"start": v(-260.7, -168.5) * mm, "mid": v(-265.1, -157.9) * mm, "end": v(-275.7, -153.5) * mm});
            skPoint(sketch, "E135.visualSharp", {"position": v(-260.7, -183.5) * mm});
            skArc(sketch, "E135.filletArc", {"start": v(-275.7, -183.5) * mm, "mid": v(-265.1, -179.1) * mm, "end": v(-260.7, -168.5) * mm});
            skSolve(sketch);
        }
        {
            var Q0;
            Q0 = qSketchRegion(id + "F35", true);
            extrude(context, id + "F36", {"entities" : qUnion([Q0]), "operationType" : NewBodyOperationType.ADD, "depth" : 19 * mm, "offsetDistance" : 25 * mm});
        }
        {
            var Q0;
            Q0=makeQuery(id+"F34.opExtrude","SWEPT_FACE",FACE,{"disambiguationData":[OSD([sQuery(id+"F33.wireOp",EDGE,"E123.MirrorCS")])]});
            var sketch = newSketch(context, id + "F37", { "sketchPlane" : qUnion([Q0])});
            skLineSegment(sketch, "E136.0.0", {"start": v(336, -133.5) * mm, "end": v(336, -112) * mm});
            skLineSegment(sketch, "E136.0.3", {"start": v(312, -51) * mm, "end": v(306, -51) * mm});
            skLineSegment(sketch, "E136.0.4", {"start": v(306, -51) * mm, "end": v(306, -133.5) * mm});
            skArc(sketch, "E136.0.5", {"start": v(306, -133.5) * mm, "mid": v(300.14, -147.64) * mm, "end": v(286, -153.5) * mm});
            skLineSegment(sketch, "E136.0.6", {"start": v(286, -153.5) * mm, "end": v(275.7, -153.5) * mm});
            skArc(sketch, "E136.0.7", {"start": v(275.7, -153.5) * mm, "mid": v(260.7, -168.5) * mm, "end": v(275.7, -183.5) * mm});
            skLineSegment(sketch, "E136.0.8", {"start": v(275.7, -183.5) * mm, "end": v(286, -183.5) * mm});
            skArc(sketch, "E136.0.9", {"start": v(286, -183.5) * mm, "mid": v(321.36, -168.86) * mm, "end": v(336, -133.5) * mm});
            skLineSegment(sketch, "E137", {"start": v(336, -112) * mm, "end": v(336, -53) * mm});
            skArc(sketch, "E138.0", {"start": v(336, -53) * mm, "mid": v(335.41, -51.59) * mm, "end": v(334, -51) * mm});
            skLineSegment(sketch, "E139.0", {"start": v(334, -51) * mm, "end": v(312, -51) * mm});
            skSolve(sketch);
        }
        {
            var Q0;
            Q0 = qSketchRegion(id + "F37", true);
            extrude(context, id + "F38", {"entities" : qUnion([Q0]), "operationType" : NewBodyOperationType.ADD, "depth" : 19 * mm, "offsetDistance" : 25 * mm});
        }
    });
